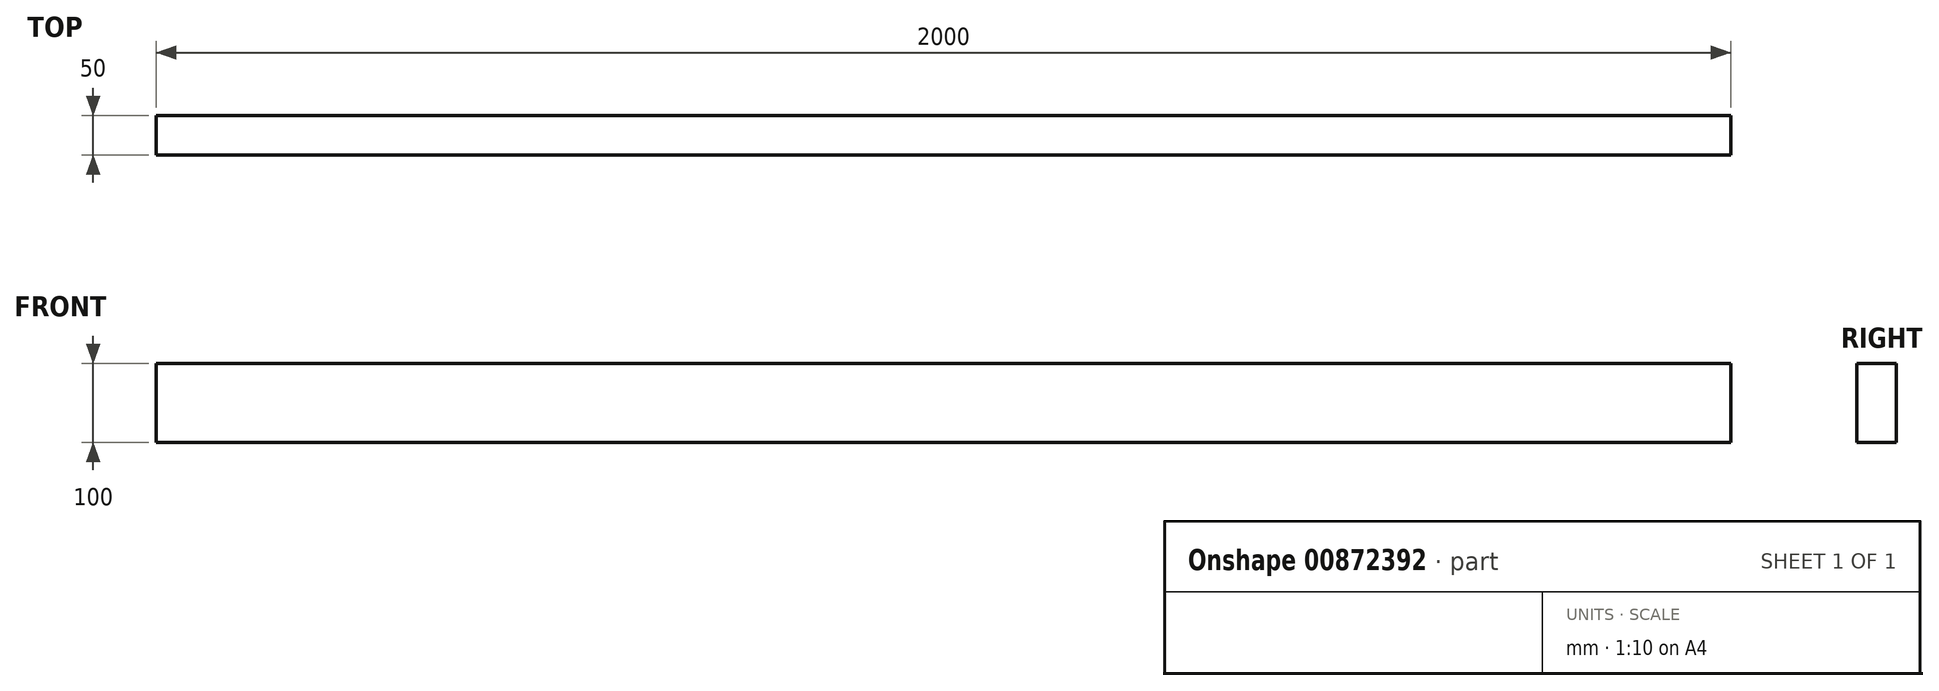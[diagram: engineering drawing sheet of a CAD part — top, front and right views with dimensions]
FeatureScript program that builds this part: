
annotation { "Feature Type Name" : "Feature", "Feature Type Description" : "" }
export const myFeature = defineFeature(function(context is Context, id is Id, definition is map)
    precondition{}
    {
        {
            var Q0;
            Q0=qCreatedBy(makeId("Right.planeOp"),FACE);
            var sketch = newSketch(context, id + "F0", { "sketchPlane" : qUnion([Q0])});
            skLineSegment(sketch, "E0.bottom", {"start": v(-25, 50) * mm, "end": v(25, 50) * mm});
            skLineSegment(sketch, "E0.top", {"start": v(-25, -50) * mm, "end": v(25, -50) * mm});
            skLineSegment(sketch, "E0.left", {"start": v(-25, 50) * mm, "end": v(-25, -50) * mm});
            skLineSegment(sketch, "E0.right", {"start": v(25, 50) * mm, "end": v(25, -50) * mm});
            skSolve(sketch);
        }
        {
            var Q0;
            Q0=qSketchRegion(id+"F0",true);
            extrude(context, id + "F1", {"entities" : qUnion([Q0]), "depth" : 2000 * mm, "offsetDistance" : 25 * mm});
        }
        {
            var Q0;
            Q0=makeQuery(id+"F1.opExtrude","SWEPT_BODY",BODY,{"disambiguationData":[OSD([sQuery(id+"F0.wireOp",EDGE,"E0.bottom"),sQuery(id+"F0.wireOp",EDGE,"E0.top"),sQuery(id+"F0.wireOp",EDGE,"E0.left"),sQuery(id+"F0.wireOp",EDGE,"E0.right")])]});
            transform(context, id + "F2", {"entities" : qUnion([Q0]), "transformType" : TransformType.TRANSLATION_3D, "dx" : 0 * mm, "dy" : 2000 * mm, "dz" : 0 * mm, "makeCopy" : true});
        }
        {
            var Q0;
            Q0=makeQuery(id+"F1.opExtrude","SWEPT_BODY",BODY,{"disambiguationData":[OSD([sQuery(id+"F0.wireOp",EDGE,"E0.bottom"),sQuery(id+"F0.wireOp",EDGE,"E0.top"),sQuery(id+"F0.wireOp",EDGE,"E0.left"),sQuery(id+"F0.wireOp",EDGE,"E0.right")])]});
            var Q1;
            Q1=makeQuery(id+"F1.opExtrude","CAP_EDGE",EDGE,{"disambiguationData":[OSD([sQuery(id+"F0.wireOp",EDGE,"E0.left")])],"isStart":true});
            transform(context, id + "F3", {"entities" : qUnion([Q0]), "transformType" : TransformType.ROTATION, "transformAxis" : qUnion([Q1]), "angle" : 90 * degree, "oppositeDirection" : true, "makeCopy" : true});
        }
        {
            var Q0;
            Q0=makeQuery(id+"F3.opPattern","COPY",BODY,{"derivedFrom":makeQuery(id+"F1.opExtrude","SWEPT_BODY",BODY,{"disambiguationData":[OSD([sQuery(id+"F0.wireOp",EDGE,"E0.bottom"),sQuery(id+"F0.wireOp",EDGE,"E0.top"),sQuery(id+"F0.wireOp",EDGE,"E0.left"),sQuery(id+"F0.wireOp",EDGE,"E0.right")])]}),"instanceName":"1"});
            deleteBodies(context, id + "F4", {"entities" : qUnion([Q0])});
        }
        {
            var Q0;
            Q0=makeQuery(id+"F1.opExtrude","SWEPT_BODY",BODY,{"disambiguationData":[OSD([sQuery(id+"F0.wireOp",EDGE,"E0.bottom"),sQuery(id+"F0.wireOp",EDGE,"E0.top"),sQuery(id+"F0.wireOp",EDGE,"E0.left"),sQuery(id+"F0.wireOp",EDGE,"E0.right")])]});
            transform(context, id + "F5", {"entities" : qUnion([Q0]), "transformType" : TransformType.TRANSLATION_3D, "dx" : 0 * mm, "dy" : 0 * mm, "dz" : 0 * mm, "makeCopy" : true});
        }
        {
            var Q0;
            Q0=makeQuery(id+"F5.opPattern","COPY",BODY,{"derivedFrom":makeQuery(id+"F1.opExtrude","SWEPT_BODY",BODY,{"disambiguationData":[OSD([sQuery(id+"F0.wireOp",EDGE,"E0.bottom"),sQuery(id+"F0.wireOp",EDGE,"E0.top"),sQuery(id+"F0.wireOp",EDGE,"E0.left"),sQuery(id+"F0.wireOp",EDGE,"E0.right")])]}),"instanceName":"1"});
            deleteBodies(context, id + "F6", {"entities" : qUnion([Q0])});
        }
        {
            var Q0;
            Q0=makeQuery(id+"F2.opPattern","COPY",BODY,{"derivedFrom":makeQuery(id+"F1.opExtrude","SWEPT_BODY",BODY,{"disambiguationData":[OSD([sQuery(id+"F0.wireOp",EDGE,"E0.bottom"),sQuery(id+"F0.wireOp",EDGE,"E0.top"),sQuery(id+"F0.wireOp",EDGE,"E0.left"),sQuery(id+"F0.wireOp",EDGE,"E0.right")])]}),"instanceName":"1"});
            deleteBodies(context, id + "F7", {"entities" : qUnion([Q0])});
        }
    });
